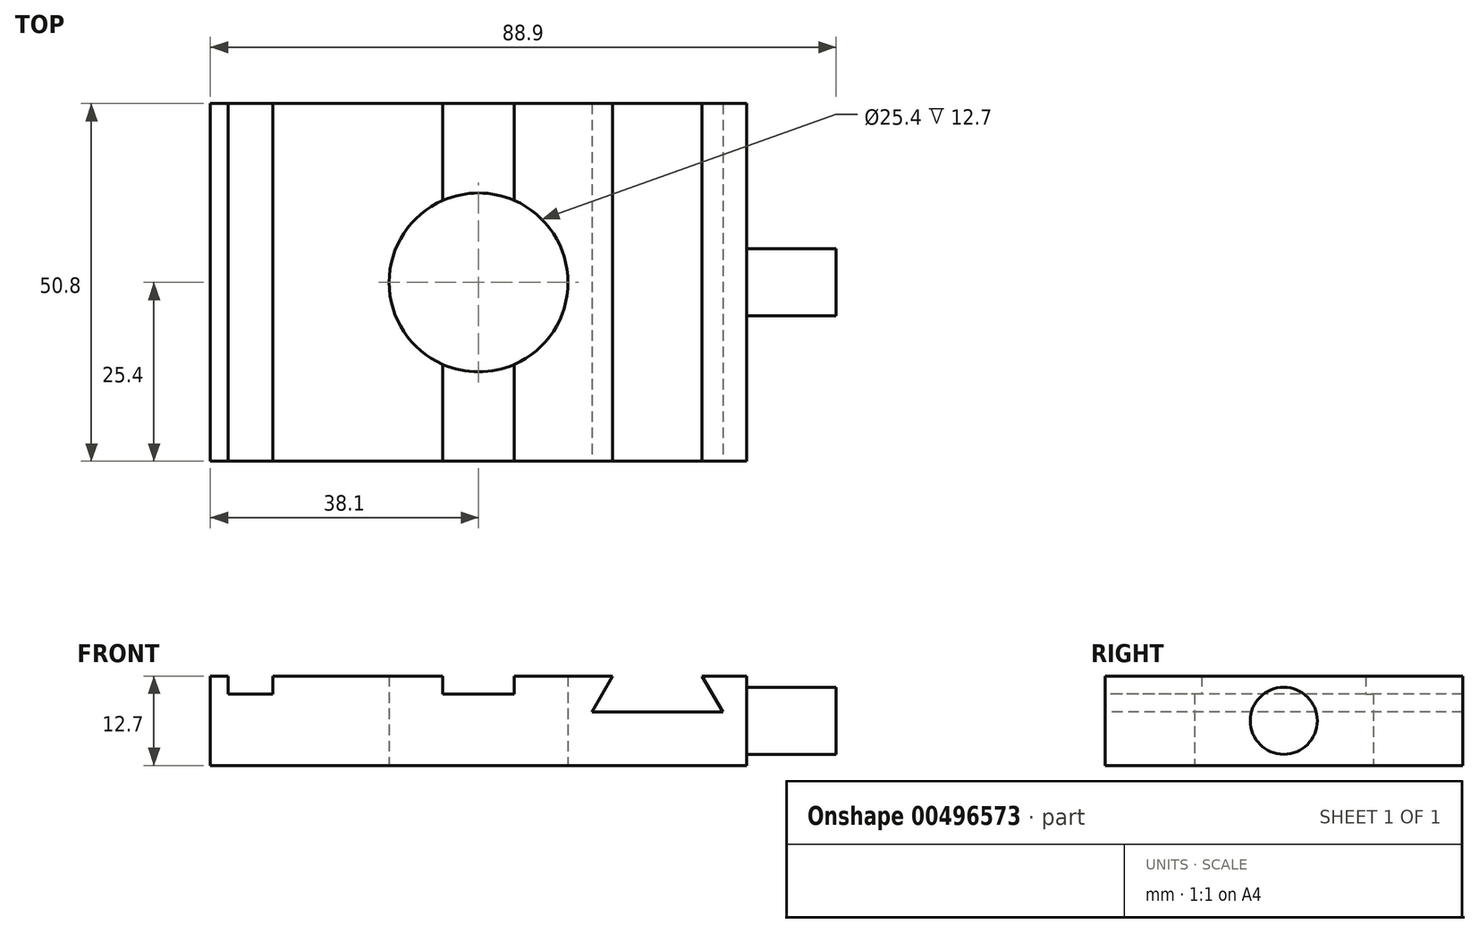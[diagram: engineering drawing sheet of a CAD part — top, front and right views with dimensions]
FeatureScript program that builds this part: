
annotation { "Feature Type Name" : "Feature", "Feature Type Description" : "" }
export const myFeature = defineFeature(function(context is Context, id is Id, definition is map)
    precondition{}
    {
        {
            var Q0;
            Q0=qCreatedBy(makeId("Top.planeOp"),FACE);
            var sketch = newSketch(context, id + "F0", { "sketchPlane" : qUnion([Q0])});
            skLineSegment(sketch, "E0.bottom", {"start": v(38.1, 25.4) * mm, "end": v(-38.1, 25.4) * mm});
            skLineSegment(sketch, "E0.top", {"start": v(38.1, -25.4) * mm, "end": v(-38.1, -25.4) * mm});
            skLineSegment(sketch, "E0.left", {"start": v(38.1, 25.4) * mm, "end": v(38.1, -25.4) * mm});
            skLineSegment(sketch, "E0.right", {"start": v(-38.1, 25.4) * mm, "end": v(-38.1, -25.4) * mm});
            skPoint(sketch, "E0.middle", {"position": v(0, 0) * mm});
            skCircle(sketch, "E1", {"center": v(0, 0) * mm, "radius": 12.7 * mm});
            skSolve(sketch);
        }
        {
            var Q0;
            Q0 = qSketchRegion(id + "F0", true);
            extrude(context, id + "F1", {"entities" : qUnion([Q0]), "depth" : 12.7 * mm, "offsetDistance" : 25.4 * mm});
        }
        {
            var Q0;
            Q0=makeQuery(id+"F1.opExtrude","CAP_FACE",FACE,{"disambiguationData":[OSD([sQuery(id+"F0.wireOp",EDGE,"E0.bottom"),sQuery(id+"F0.wireOp",EDGE,"E0.top"),sQuery(id+"F0.wireOp",EDGE,"E0.left"),sQuery(id+"F0.wireOp",EDGE,"E0.right"),sQuery(id+"F0.wireOp",EDGE,"E1")])],"isStart":false});
            var sketch = newSketch(context, id + "F2", { "sketchPlane" : qUnion([Q0])});
            skLineSegment(sketch, "E2.bottom", {"start": v(-35.56, 25.4) * mm, "end": v(-29.21, 25.4) * mm});
            skLineSegment(sketch, "E2.top", {"start": v(-35.56, -25.4) * mm, "end": v(-29.21, -25.4) * mm});
            skLineSegment(sketch, "E2.left", {"start": v(-35.56, 25.4) * mm, "end": v(-35.56, -25.4) * mm});
            skLineSegment(sketch, "E2.right", {"start": v(-29.21, 25.4) * mm, "end": v(-29.21, -25.4) * mm});
            skLineSegment(sketch, "E3.bottom", {"start": v(-5.08, 25.4) * mm, "end": v(5.08, 25.4) * mm});
            skLineSegment(sketch, "E3.top", {"start": v(-5.08, -25.4) * mm, "end": v(5.08, -25.4) * mm});
            skLineSegment(sketch, "E3.left", {"start": v(-5.08, 25.4) * mm, "end": v(-5.08, -25.4) * mm});
            skLineSegment(sketch, "E3.right", {"start": v(5.08, 25.4) * mm, "end": v(5.08, -25.4) * mm});
            skPoint(sketch, "E4", {"position": v(0, 0) * mm});
            skLineSegment(sketch, "E5", {"start": v(0, 25.4) * mm, "end": v(0, -25.4) * mm, "construction": true});
            skSolve(sketch);
        }
        {
            var Q0;
            Q0 = qSketchRegion(id + "F2", true);
            extrude(context, id + "F3", {"entities" : qUnion([Q0]), "operationType" : NewBodyOperationType.REMOVE, "oppositeDirection" : true, "depth" : 2.54 * mm, "offsetDistance" : 25.4 * mm});
        }
        {
            var Q0;
            Q0=makeQuery(id+"F1.opExtrude","SWEPT_FACE",FACE,{"disambiguationData":[OSD([sQuery(id+"F0.wireOp",EDGE,"E0.top")])]});
            var sketch = newSketch(context, id + "F4", { "sketchPlane" : qUnion([Q0])});
            skLineSegment(sketch, "E6", {"start": v(19.05, 12.7) * mm, "end": v(16.12, 7.62) * mm});
            skLineSegment(sketch, "E7", {"start": v(16.12, 7.62) * mm, "end": v(34.68, 7.62) * mm});
            skLineSegment(sketch, "E8", {"start": v(34.68, 7.62) * mm, "end": v(31.75, 12.7) * mm});
            skLineSegment(sketch, "E9", {"start": v(31.75, 12.7) * mm, "end": v(19.05, 12.7) * mm});
            skLineSegment(sketch, "E10", {"start": v(25.4, 7.62) * mm, "end": v(25.4, 12.7) * mm, "construction": true});
            skSolve(sketch);
        }
        {
            var Q0;
            Q0=makeQuery(id+"F4.imprint","IMPRINT",FACE,{"disambiguationData":[TD([[makeQuery(id+"F4.imprint","IMPRINT",EDGE,{"derivedFrom":sQuery(id+"F4.wireOp",EDGE,"E6")}),1.0]])]});
            extrude(context, id + "F5", {"entities" : qUnion([Q0]), "operationType" : NewBodyOperationType.REMOVE, "endBound" : BoundingType.UP_TO_NEXT, "oppositeDirection" : true, "depth" : 25.4 * mm, "offsetDistance" : 25.4 * mm});
        }
        {
            var Q0;
            Q0=makeQuery(id+"F1.opExtrude","SWEPT_FACE",FACE,{"disambiguationData":[OSD([sQuery(id+"F0.wireOp",EDGE,"E0.left")])]});
            var sketch = newSketch(context, id + "F6", { "sketchPlane" : qUnion([Q0])});
            skCircle(sketch, "E11", {"center": v(0, 6.35) * mm, "radius": 4.76 * mm});
            skPoint(sketch, "E11.centerSnap0", {"position": v(-25.4, 6.35) * mm});
            skPoint(sketch, "E11.centerSnap1", {"position": v(0, 12.7) * mm});
            skSolve(sketch);
        }
        {
            var Q0;
            Q0=makeQuery(id+"F6.imprint","IMPRINT",FACE,{"disambiguationData":[TD([[makeQuery(id+"F6.imprint","IMPRINT",EDGE,{"derivedFrom":sQuery(id+"F6.wireOp",EDGE,"E11")}),1.0]])]});
            extrude(context, id + "F7", {"entities" : qUnion([Q0]), "operationType" : NewBodyOperationType.ADD, "depth" : 12.7 * mm, "offsetDistance" : 25.4 * mm});
        }
    });
